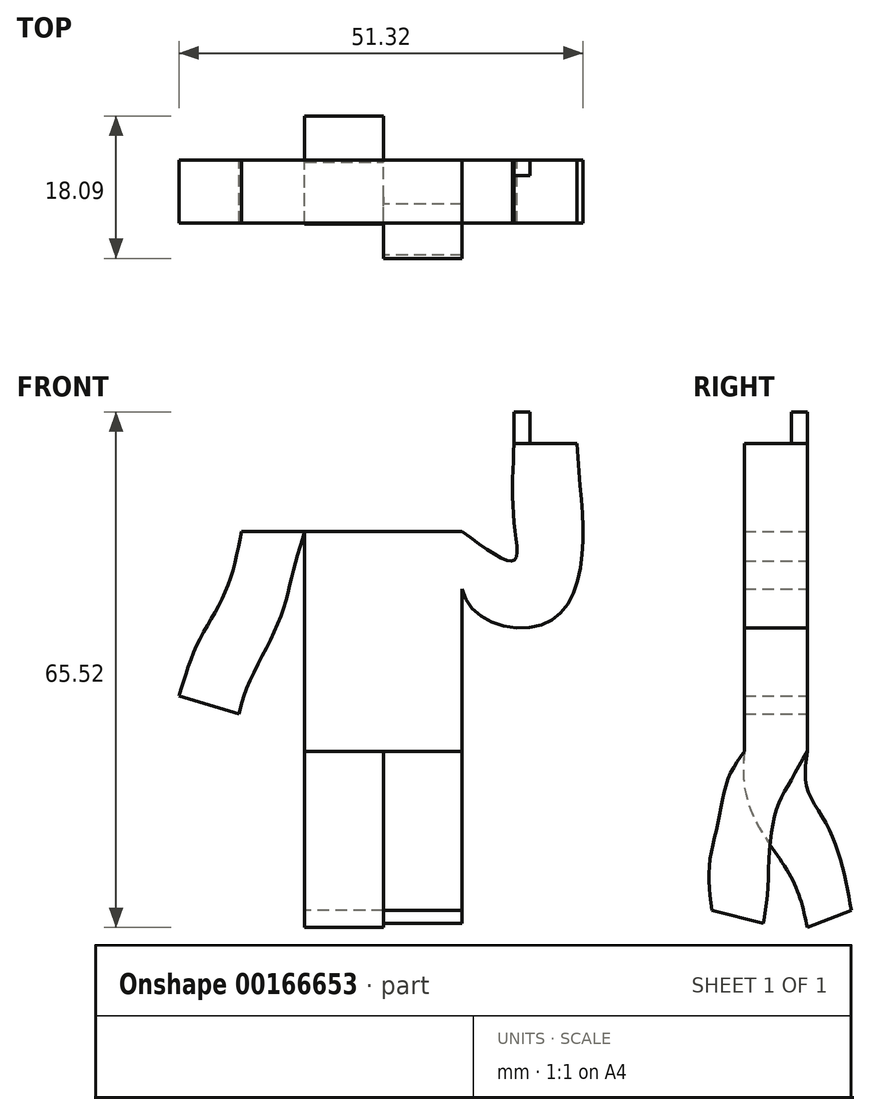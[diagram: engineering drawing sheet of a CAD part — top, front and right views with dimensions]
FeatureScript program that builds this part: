
annotation { "Feature Type Name" : "Feature", "Feature Type Description" : "" }
export const myFeature = defineFeature(function(context is Context, id is Id, definition is map)
    precondition{}
    {
        {
            var Q0;
            Q0=qCreatedBy(makeId("Front.planeOp"),FACE);
            var sketch = newSketch(context, id + "F0", { "sketchPlane" : qUnion([Q0])});
            skLineSegment(sketch, "E0.bottom", {"start": v(-10, 14) * mm, "end": v(10, 14) * mm});
            skLineSegment(sketch, "E0.top", {"start": v(-10, -14) * mm, "end": v(10, -14) * mm});
            skLineSegment(sketch, "E0.left", {"start": v(-10, 14) * mm, "end": v(-10, -14) * mm});
            skLineSegment(sketch, "E0.right", {"start": v(10, 14) * mm, "end": v(10, -14) * mm});
            skPoint(sketch, "E0.middle", {"position": v(0, 0) * mm});
            skFitSpline(sketch, "E1", {"points": [v(10, 14) * mm, v(11.37, 4.06) * mm, v(20.93, 2.44) * mm, v(25.26, 11.46) * mm, v(24.6, 25.17) * mm], "startDerivative": vector(-5, -47.56) * mm, "endDerivative": vector(-1.96, 49.13) * mm});
            skFitSpline(sketch, "E2", {"points": [v(16.6, 25.17) * mm, v(16.6, 15.17) * mm, v(16.6, 10.3) * mm, v(10, 14) * mm], "startDerivative": vector(-1.34, -26.1) * mm, "endDerivative": vector(-25.14, 18.85) * mm});
            skFitSpline(sketch, "E3", {"points": [v(-10, 14) * mm, v(-11.55, 8.57) * mm, v(-12.99, 3.34) * mm, v(-15.88, -2.8) * mm, v(-18.31, -9.23) * mm], "startDerivative": vector(-6.96, -22.84) * mm, "endDerivative": vector(-4.47, -25.71) * mm});
            skLineSegment(sketch, "E4", {"start": v(-18.31, -9.23) * mm, "end": v(-25.98, -6.95) * mm});
            skFitSpline(sketch, "E5", {"points": [v(-25.98, -6.95) * mm, v(-23.45, 0) * mm, v(-20.03, 6.4) * mm, v(-18.04, 13.98) * mm], "startDerivative": vector(6.57, 21.55) * mm, "endDerivative": vector(4.38, 23.07) * mm});
            skLineSegment(sketch, "E6", {"start": v(-18.04, 13.98) * mm, "end": v(-10, 14) * mm});
            skLineSegment(sketch, "E7", {"start": v(-18.04, 13.98) * mm, "end": v(10, 14) * mm});
            skPoint(sketch, "E8.end.orphan", {"position": v(18.6, 25.17) * mm});
            skLineSegment(sketch, "E9", {"start": v(24.6, 25.17) * mm, "end": v(16.6, 25.17) * mm});
            skSolve(sketch);
        }
        {
            var Q0;
            Q0 = qSketchRegion(id + "F0", true);
            extrude(context, id + "F1", {"entities" : qUnion([Q0]), "depth" : 8 * mm});
        }
        {
            var Q0;
            Q0=makeQuery(id+"F1.opExtrude","SWEPT_FACE",FACE,{"disambiguationData":[OSD([sQuery(id+"F0.wireOp",EDGE,"E0.left")])]});
            var sketch = newSketch(context, id + "F2", { "sketchPlane" : qUnion([Q0])});
            skLineSegment(sketch, "E10", {"start": v(0, -14) * mm, "end": v(8, -14) * mm});
            skFitSpline(sketch, "E11", {"points": [v(8, -14) * mm, v(8, -18.31) * mm, v(5.95, -23.9) * mm, v(1.8, -30.4) * mm, v(0, -36.35) * mm], "startDerivative": vector(1.5, -19.82) * mm, "endDerivative": vector(-4.84, -23.49) * mm});
            skFitSpline(sketch, "E12", {"points": [v(0, -14) * mm, v(0, -18.67) * mm, v(-2.35, -23) * mm, v(-4.51, -28.78) * mm, v(-5.6, -34.19) * mm], "startDerivative": vector(2.62, -20.66) * mm, "endDerivative": vector(-3.56, -20.88) * mm});
            skLineSegment(sketch, "E13", {"start": v(-5.6, -34.19) * mm, "end": v(0, -36.35) * mm});
            skSolve(sketch);
        }
        {
            var Q0;
            Q0 = qSketchRegion(id + "F2", true);
            extrude(context, id + "F3", {"entities" : qUnion([Q0]), "operationType" : NewBodyOperationType.ADD, "oppositeDirection" : true, "depth" : 10 * mm});
        }
        {
            var Q0;
            Q0=makeQuery(id+"F3.opExtrude","CAP_FACE",FACE,{"disambiguationData":[OSD([sQuery(id+"F2.wireOp",EDGE,"E10"),sQuery(id+"F2.wireOp",EDGE,"E11"),sQuery(id+"F2.wireOp",EDGE,"E12"),sQuery(id+"F2.wireOp",EDGE,"E13")])],"isStart":false});
            var sketch = newSketch(context, id + "F4", { "sketchPlane" : qUnion([Q0])});
            skPoint(sketch, "E14.2.internal.snap0", {"position": v(-4, -14) * mm});
            skLineSegment(sketch, "E15", {"start": v(0, -14) * mm, "end": v(-8, -14) * mm});
            skPoint(sketch, "E16.5.internal.orphan", {"position": v(-11.19, -36.35) * mm});
            skFitSpline(sketch, "E17", {"points": [v(0, -14) * mm, v(-2.35, -18.13) * mm, v(-3.79, -21.02) * mm, v(-4.72, -25.83) * mm, v(-5.05, -32.02) * mm, v(-5.6, -35.81) * mm], "startDerivative": vector(-12.06, -21.38) * mm, "endDerivative": vector(-3.45, -19.1) * mm});
            skFitSpline(sketch, "E18", {"points": [v(0, -14) * mm, v(-0.82, -15.46) * mm], "startDerivative": vector(-0.82, -1.46) * mm, "endDerivative": vector(-0.82, -1.46) * mm});
            skFitSpline(sketch, "E19", {"points": [v(-8, -14) * mm, v(-10.1, -17.6) * mm, v(-11.37, -23.18) * mm, v(-12.45, -28.6) * mm, v(-12.09, -34.19) * mm], "startDerivative": vector(-10.63, -14.77) * mm, "endDerivative": vector(2.95, -21.88) * mm});
            skLineSegment(sketch, "E20", {"start": v(-12.09, -34.19) * mm, "end": v(-5.6, -35.81) * mm});
            skLineSegment(sketch, "E21", {"start": v(-8, -14) * mm, "end": v(-8.79, -15.1) * mm});
            skSolve(sketch);
        }
        {
            var Q0;
            Q0 = qSketchRegion(id + "F4", true);
            extrude(context, id + "F5", {"entities" : qUnion([Q0]), "operationType" : NewBodyOperationType.ADD, "depth" : 10 * mm});
        }
        {
            var Q0;
            Q0=makeQuery(id+"F1.opExtrude","CAP_FACE",FACE,{"disambiguationData":[OSD([sQuery(id+"F0.wireOp",EDGE,"E0.bottom"),sQuery(id+"F0.wireOp",EDGE,"E0.top"),sQuery(id+"F0.wireOp",EDGE,"E0.left"),sQuery(id+"F0.wireOp",EDGE,"E0.right"),sQuery(id+"F0.wireOp",EDGE,"E1"),sQuery(id+"F0.wireOp",EDGE,"E2"),sQuery(id+"F0.wireOp",EDGE,"E3"),sQuery(id+"F0.wireOp",EDGE,"E4"),sQuery(id+"F0.wireOp",EDGE,"E5"),sQuery(id+"F0.wireOp",EDGE,"E6"),sQuery(id+"F0.wireOp",EDGE,"E7"),sQuery(id+"F0.wireOp",EDGE,"E9")])],"isStart":true});
            var sketch = newSketch(context, id + "F6", { "sketchPlane" : qUnion([Q0])});
            skLineSegment(sketch, "E22", {"start": v(-16.6, 25.17) * mm, "end": v(-16.6, 29.17) * mm});
            skLineSegment(sketch, "E23", {"start": v(-16.6, 25.17) * mm, "end": v(-18.6, 25.17) * mm});
            skLineSegment(sketch, "E24", {"start": v(-18.6, 25.17) * mm, "end": v(-18.6, 29.17) * mm});
            skLineSegment(sketch, "E25", {"start": v(-18.6, 29.17) * mm, "end": v(-16.6, 29.17) * mm});
            skSolve(sketch);
        }
        {
            var Q0;
            Q0 = qSketchRegion(id + "F6", true);
            extrude(context, id + "F7", {"entities" : qUnion([Q0]), "operationType" : NewBodyOperationType.ADD, "oppositeDirection" : true, "depth" : 2 * mm});
        }
    });
